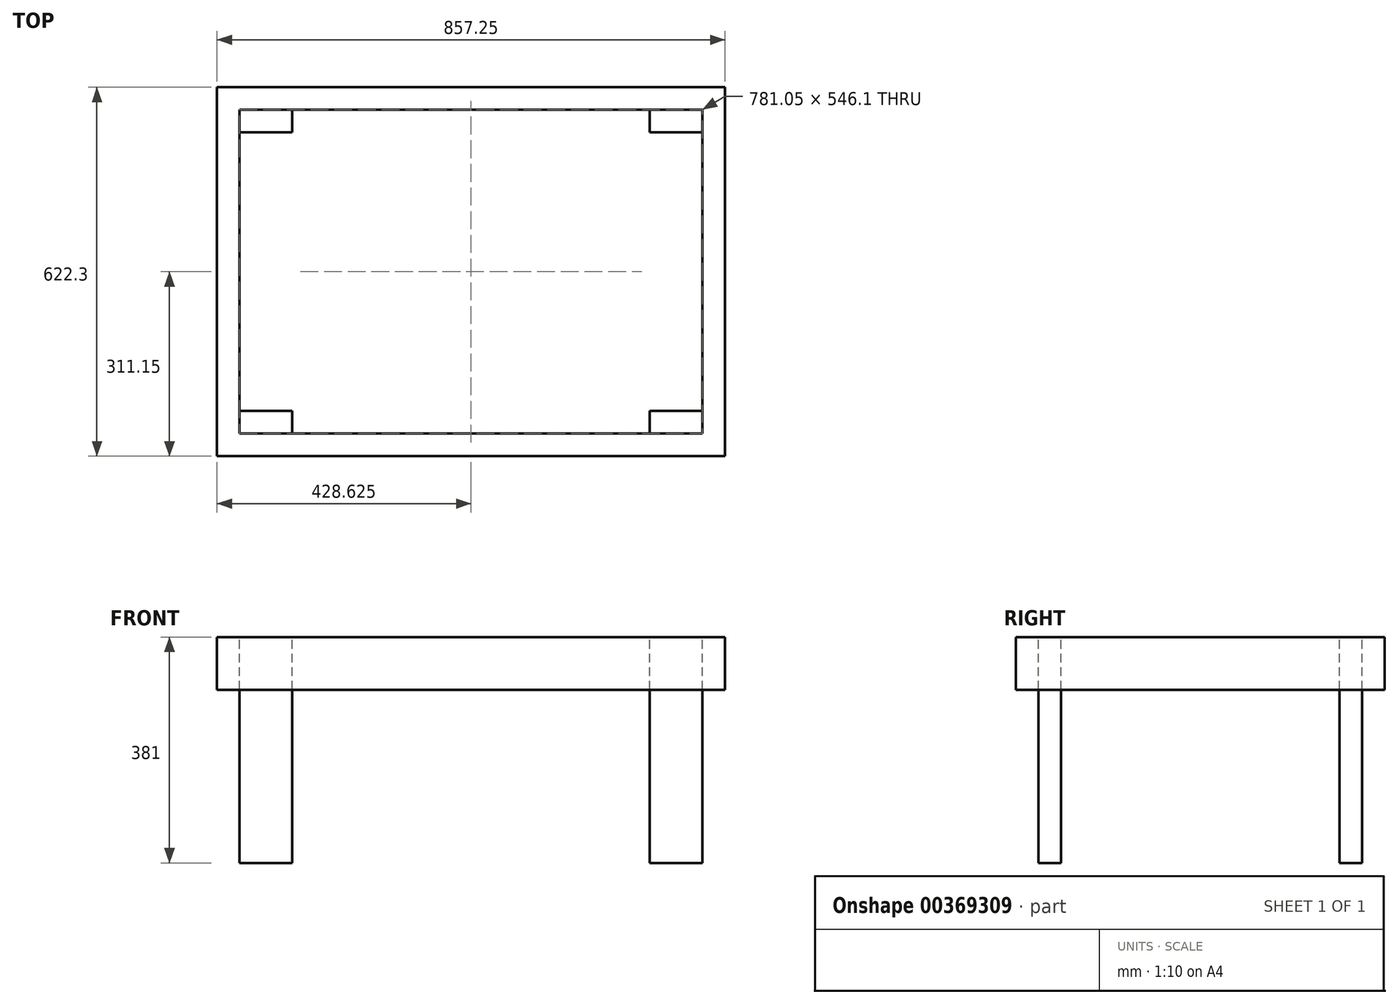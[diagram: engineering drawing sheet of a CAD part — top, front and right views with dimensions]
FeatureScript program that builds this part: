
annotation { "Feature Type Name" : "Feature", "Feature Type Description" : "" }
export const myFeature = defineFeature(function(context is Context, id is Id, definition is map)
    precondition{}
    {
        {
            var Q0;
            Q0=qCreatedBy(makeId("Top.planeOp"),FACE);
            var sketch = newSketch(context, id + "F0", { "sketchPlane" : qUnion([Q0])});
            skLineSegment(sketch, "E0.bottom", {"start": v(438.15, -330.2) * mm, "end": v(-438.15, -330.2) * mm, "construction": true});
            skLineSegment(sketch, "E0.top", {"start": v(438.15, 330.2) * mm, "end": v(-438.15, 330.2) * mm, "construction": true});
            skLineSegment(sketch, "E0.left", {"start": v(438.15, -330.2) * mm, "end": v(438.15, 330.2) * mm, "construction": true});
            skLineSegment(sketch, "E0.right", {"start": v(-438.15, -330.2) * mm, "end": v(-438.15, 330.2) * mm, "construction": true});
            skPoint(sketch, "E0.middle", {"position": v(0, 0) * mm});
            skLineSegment(sketch, "E1", {"start": v(-406.4, 279.4) * mm, "end": v(412.75, 279.4) * mm, "construction": true});
            skLineSegment(sketch, "E2", {"start": v(412.75, 279.4) * mm, "end": v(412.75, -304.8) * mm, "construction": true});
            skLineSegment(sketch, "E3", {"start": v(412.75, -304.8) * mm, "end": v(-406.4, -304.8) * mm, "construction": true});
            skLineSegment(sketch, "E4", {"start": v(-406.4, -304.8) * mm, "end": v(-406.4, 279.4) * mm, "construction": true});
            skLineSegment(sketch, "E5.0", {"start": v(-387.35, 260.35) * mm, "end": v(393.7, 260.35) * mm});
            skLineSegment(sketch, "E5.1", {"start": v(-387.35, -285.75) * mm, "end": v(-387.35, 260.35) * mm});
            skLineSegment(sketch, "E5.2", {"start": v(393.7, -285.75) * mm, "end": v(-387.35, -285.75) * mm});
            skLineSegment(sketch, "E5.3", {"start": v(393.7, 260.35) * mm, "end": v(393.7, -285.75) * mm});
            skLineSegment(sketch, "E6.0", {"start": v(-425.45, 298.45) * mm, "end": v(431.8, 298.45) * mm});
            skLineSegment(sketch, "E6.1", {"start": v(-425.45, -323.85) * mm, "end": v(-425.45, 298.45) * mm});
            skLineSegment(sketch, "E6.2", {"start": v(431.8, -323.85) * mm, "end": v(-425.45, -323.85) * mm});
            skLineSegment(sketch, "E6.3", {"start": v(431.8, 298.45) * mm, "end": v(431.8, -323.85) * mm});
            skSolve(sketch);
        }
        {
            var Q0;
            Q0=makeQuery(id+"F0.imprint","IMPRINT",FACE,{"disambiguationData":[TD([[makeQuery(id+"F0.imprint","IMPRINT",EDGE,{"derivedFrom":sQuery(id+"F0.wireOp",EDGE,"E5.0")}),1.0]])]});
            extrude(context, id + "F1", {"entities" : qUnion([Q0]), "depth" : 88.9 * mm});
        }
        {
            var Q0;
            Q0=makeQuery(id+"F1.opExtrude","CAP_FACE",FACE,{"disambiguationData":[OSD([sQuery(id+"F0.wireOp",EDGE,"E5.0"),sQuery(id+"F0.wireOp",EDGE,"E5.1"),sQuery(id+"F0.wireOp",EDGE,"E5.2"),sQuery(id+"F0.wireOp",EDGE,"E5.3"),sQuery(id+"F0.wireOp",EDGE,"E6.0"),sQuery(id+"F0.wireOp",EDGE,"E6.1"),sQuery(id+"F0.wireOp",EDGE,"E6.2"),sQuery(id+"F0.wireOp",EDGE,"E6.3")])],"isStart":false});
            var sketch = newSketch(context, id + "F2", { "sketchPlane" : qUnion([Q0])});
            skLineSegment(sketch, "E7.bottom", {"start": v(-387.35, -285.75) * mm, "end": v(-298.45, -285.75) * mm});
            skLineSegment(sketch, "E7.top", {"start": v(-387.35, -247.65) * mm, "end": v(-298.45, -247.65) * mm});
            skLineSegment(sketch, "E7.left", {"start": v(-387.35, -285.75) * mm, "end": v(-387.35, -247.65) * mm});
            skLineSegment(sketch, "E7.right", {"start": v(-298.45, -285.75) * mm, "end": v(-298.45, -247.65) * mm});
            skLineSegment(sketch, "E8", {"start": v(-387.35, -12.7) * mm, "end": v(393.7, -12.7) * mm, "construction": true});
            skLineSegment(sketch, "E9.MirrorCS", {"start": v(-387.35, 222.25) * mm, "end": v(-298.45, 222.25) * mm});
            skLineSegment(sketch, "E10.MirrorCS", {"start": v(-387.35, 260.35) * mm, "end": v(-387.35, 222.25) * mm});
            skLineSegment(sketch, "E11.MirrorCS", {"start": v(-387.35, 260.35) * mm, "end": v(-298.45, 260.35) * mm});
            skLineSegment(sketch, "E12.MirrorCS", {"start": v(-298.45, 260.35) * mm, "end": v(-298.45, 222.25) * mm});
            skLineSegment(sketch, "E13", {"start": v(3.18, -285.75) * mm, "end": v(3.17, 260.35) * mm, "construction": true});
            skLineSegment(sketch, "E14.MirrorCS", {"start": v(393.7, 260.35) * mm, "end": v(304.8, 260.35) * mm});
            skLineSegment(sketch, "E15.MirrorCS", {"start": v(304.8, 260.35) * mm, "end": v(304.8, 222.25) * mm});
            skLineSegment(sketch, "E16.MirrorCS", {"start": v(393.7, 260.35) * mm, "end": v(393.7, 222.25) * mm});
            skLineSegment(sketch, "E17.MirrorCS", {"start": v(393.7, 222.25) * mm, "end": v(304.8, 222.25) * mm});
            skLineSegment(sketch, "E18.MirrorCS", {"start": v(304.8, -285.75) * mm, "end": v(304.8, -247.65) * mm});
            skLineSegment(sketch, "E19.MirrorCS", {"start": v(393.7, -285.75) * mm, "end": v(393.7, -247.65) * mm});
            skLineSegment(sketch, "E20.MirrorCS", {"start": v(393.7, -247.65) * mm, "end": v(304.8, -247.65) * mm});
            skLineSegment(sketch, "E21.MirrorCS", {"start": v(393.7, -285.75) * mm, "end": v(304.8, -285.75) * mm});
            skSolve(sketch);
        }
        {
            var Q0;
            Q0=makeQuery(id+"F2.imprint","IMPRINT",FACE,{"disambiguationData":[TD([[makeQuery(id+"F2.imprint","IMPRINT",EDGE,{"derivedFrom":sQuery(id+"F2.wireOp",EDGE,"E9.MirrorCS")}),1.0]])]});
            var Q1;
            Q1=makeQuery(id+"F2.imprint","IMPRINT",FACE,{"disambiguationData":[TD([[makeQuery(id+"F2.imprint","IMPRINT",EDGE,{"derivedFrom":sQuery(id+"F2.wireOp",EDGE,"E7.bottom")}),-1.0]])]});
            var Q2;
            Q2=makeQuery(id+"F2.imprint","IMPRINT",FACE,{"disambiguationData":[TD([[makeQuery(id+"F2.imprint","IMPRINT",EDGE,{"derivedFrom":sQuery(id+"F2.wireOp",EDGE,"E18.MirrorCS")}),-1.0]])]});
            var Q3;
            Q3=makeQuery(id+"F2.imprint","IMPRINT",FACE,{"disambiguationData":[TD([[makeQuery(id+"F2.imprint","IMPRINT",EDGE,{"derivedFrom":sQuery(id+"F2.wireOp",EDGE,"E14.MirrorCS")}),-1.0]])]});
            var Q4;
            Q4=sQuery(id+"F2.wireOp",EDGE,"E7.top");
            var Q5;
            Q5=sQuery(id+"F2.wireOp",EDGE,"E7.right");
            var Q6;
            Q6=sQuery(id+"F2.wireOp",EDGE,"E7.left");
            var Q7;
            Q7=sQuery(id+"F2.wireOp",EDGE,"E7.bottom");
            var Q8;
            Q8=sQuery(id+"F2.wireOp",EDGE,"E10.MirrorCS");
            var Q9;
            Q9=sQuery(id+"F2.wireOp",EDGE,"E9.MirrorCS");
            var Q10;
            Q10=sQuery(id+"F2.wireOp",EDGE,"E11.MirrorCS");
            var Q11;
            Q11=sQuery(id+"F2.wireOp",EDGE,"E12.MirrorCS");
            extrude(context, id + "F3", {"entities" : qUnion([Q0, Q1, Q2, Q3]), "surfaceEntities" : qUnion([Q4, Q5, Q6, Q7, Q8, Q9, Q10, Q11]), "oppositeDirection" : true, "depth" : 381 * mm});
        }
    });
